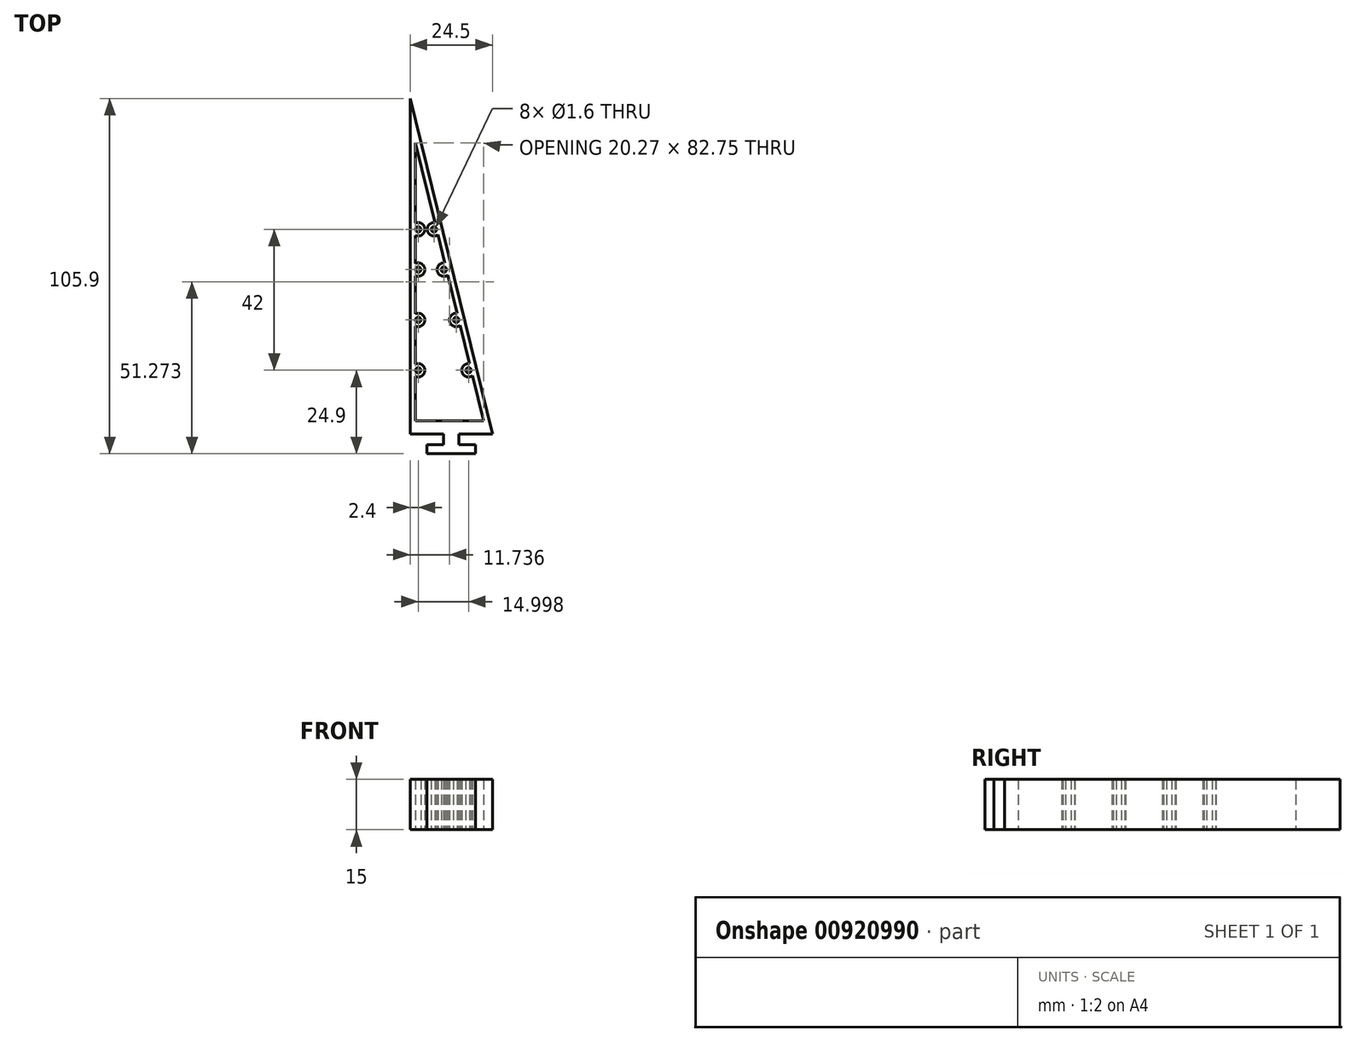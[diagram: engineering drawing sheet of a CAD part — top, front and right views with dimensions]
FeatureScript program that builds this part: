
annotation { "Feature Type Name" : "Feature", "Feature Type Description" : "" }
export const myFeature = defineFeature(function(context is Context, id is Id, definition is map)
    precondition{}
    {
        {
            var Q0;
            Q0=qCreatedBy(makeId("Top.planeOp"),FACE);
            var sketch = newSketch(context, id + "F0", { "sketchPlane" : qUnion([Q0])});
            skLineSegment(sketch, "E0", {"start": v(0, 0) * mm, "end": v(14.5, 0) * mm});
            skLineSegment(sketch, "E1", {"start": v(14.5, 0) * mm, "end": v(14.5, 2.7) * mm});
            skLineSegment(sketch, "E2", {"start": v(14.5, 2.7) * mm, "end": v(9.5, 2.7) * mm});
            skLineSegment(sketch, "E3", {"start": v(0, 0) * mm, "end": v(0, 2.7) * mm});
            skLineSegment(sketch, "E4", {"start": v(0, 2.7) * mm, "end": v(5, 2.7) * mm});
            skLineSegment(sketch, "E5", {"start": v(5, 2.7) * mm, "end": v(5, 5.9) * mm});
            skLineSegment(sketch, "E6", {"start": v(9.5, 2.7) * mm, "end": v(9.5, 5.9) * mm});
            skLineSegment(sketch, "E7", {"start": v(9.5, 5.9) * mm, "end": v(19.5, 5.9) * mm});
            skLineSegment(sketch, "E8", {"start": v(5, 5.9) * mm, "end": v(-5, 5.9) * mm});
            skLineSegment(sketch, "E9", {"start": v(-5, 5.9) * mm, "end": v(-5, 105.9) * mm});
            skLineSegment(sketch, "E10", {"start": v(-5, 105.9) * mm, "end": v(19.5, 5.9) * mm});
            skLineSegment(sketch, "E11.0", {"start": v(-3.4, 9.9) * mm, "end": v(-3.4, 23.07) * mm});
            skLineSegment(sketch, "E12.0", {"start": v(-3.4, 92.65) * mm, "end": v(0.8, 75.49) * mm});
            skLineSegment(sketch, "E13", {"start": v(16.87, 9.9) * mm, "end": v(-3.4, 9.9) * mm});
            skLineSegment(sketch, "E14", {"start": v(-3.4, 24.9) * mm, "end": v(13.2, 24.9) * mm, "construction": true});
            skLineSegment(sketch, "E15", {"start": v(-3.4, 39.9) * mm, "end": v(9.52, 39.9) * mm, "construction": true});
            skLineSegment(sketch, "E16", {"start": v(-3.4, 54.9) * mm, "end": v(5.85, 54.9) * mm, "construction": true});
            skLineSegment(sketch, "E17", {"start": v(-3.4, 66.9) * mm, "end": v(2.9, 66.9) * mm, "construction": true});
            skLineSegment(sketch, "E18", {"start": v(-3.4, 76.9) * mm, "end": v(0.46, 76.9) * mm, "construction": true});
            skCircle(sketch, "E19", {"center": v(-2.6, 24.9) * mm, "radius": 0.8 * mm});
            skArc(sketch, "E20", {"start": v(-3.4, 23.07) * mm, "mid": v(-0.6, 24.9) * mm, "end": v(-3.4, 26.73) * mm});
            skCircle(sketch, "E21", {"center": v(12.4, 24.9) * mm, "radius": 0.8 * mm});
            skArc(sketch, "E22", {"start": v(12.71, 26.87) * mm, "mid": v(10.46, 24.42) * mm, "end": v(13.6, 23.3) * mm});
            skCircle(sketch, "E23", {"center": v(-2.6, 39.9) * mm, "radius": 0.8 * mm});
            skArc(sketch, "E24", {"start": v(-3.4, 38.07) * mm, "mid": v(-0.6, 39.9) * mm, "end": v(-3.4, 41.73) * mm});
            skCircle(sketch, "E25", {"center": v(8.72, 39.9) * mm, "radius": 0.8 * mm});
            skArc(sketch, "E26", {"start": v(9.04, 41.87) * mm, "mid": v(6.78, 39.42) * mm, "end": v(9.92, 38.3) * mm});
            skCircle(sketch, "E27", {"center": v(-2.6, 54.9) * mm, "radius": 0.8 * mm});
            skArc(sketch, "E28", {"start": v(-3.4, 53.07) * mm, "mid": v(-0.6, 54.9) * mm, "end": v(-3.4, 56.73) * mm});
            skCircle(sketch, "E29", {"center": v(5.05, 54.9) * mm, "radius": 0.8 * mm});
            skArc(sketch, "E30", {"start": v(5.36, 56.87) * mm, "mid": v(3.1, 54.42) * mm, "end": v(6.24, 53.3) * mm});
            skCircle(sketch, "E31", {"center": v(-2.6, 66.9) * mm, "radius": 0.8 * mm});
            skArc(sketch, "E32", {"start": v(-3.4, 65.07) * mm, "mid": v(-0.6, 66.9) * mm, "end": v(-3.4, 68.73) * mm});
            skCircle(sketch, "E33", {"center": v(2.1, 66.9) * mm, "radius": 0.8 * mm});
            skArc(sketch, "E34", {"start": v(2.42, 68.87) * mm, "mid": v(0.17, 66.42) * mm, "end": v(3.3, 65.3) * mm});
            skLineSegment(sketch, "E35.trimOffspring", {"start": v(-3.4, 75.38) * mm, "end": v(-3.4, 92.65) * mm});
            skLineSegment(sketch, "E36.trimOffspring", {"start": v(1.51, 72.6) * mm, "end": v(2.42, 68.87) * mm});
            skLineSegment(sketch, "E37.trimOffspring", {"start": v(-3.4, 68.73) * mm, "end": v(-3.4, 72.42) * mm});
            skLineSegment(sketch, "E38.trimOffspring", {"start": v(3.3, 65.3) * mm, "end": v(5.36, 56.87) * mm});
            skLineSegment(sketch, "E39.trimOffspring", {"start": v(-3.4, 56.73) * mm, "end": v(-3.4, 65.07) * mm});
            skLineSegment(sketch, "E40.trimOffspring", {"start": v(6.24, 53.3) * mm, "end": v(9.04, 41.87) * mm});
            skLineSegment(sketch, "E41.trimOffspring", {"start": v(9.92, 38.3) * mm, "end": v(12.71, 26.87) * mm});
            skLineSegment(sketch, "E42.trimOffspring", {"start": v(13.6, 23.3) * mm, "end": v(16.87, 9.9) * mm});
            skLineSegment(sketch, "E43.trimOffspring", {"start": v(-3.4, 26.73) * mm, "end": v(-3.4, 38.07) * mm});
            skLineSegment(sketch, "E44.trimOffspring", {"start": v(-3.4, 41.73) * mm, "end": v(-3.4, 53.07) * mm});
            skLineSegment(sketch, "E45", {"start": v(-3.4, 75.38) * mm, "end": v(-3.4, 72.42) * mm});
            skLineSegment(sketch, "E46", {"start": v(0.8, 75.49) * mm, "end": v(1.51, 72.6) * mm});
            skSolve(sketch);
        }
        {
            var Q0;
            Q0 = qSketchRegion(id + "F0", true);
            extrude(context, id + "F1", {"entities" : qUnion([Q0]), "depth" : 15 * mm, "offsetDistance" : 25 * mm});
        }
    });
